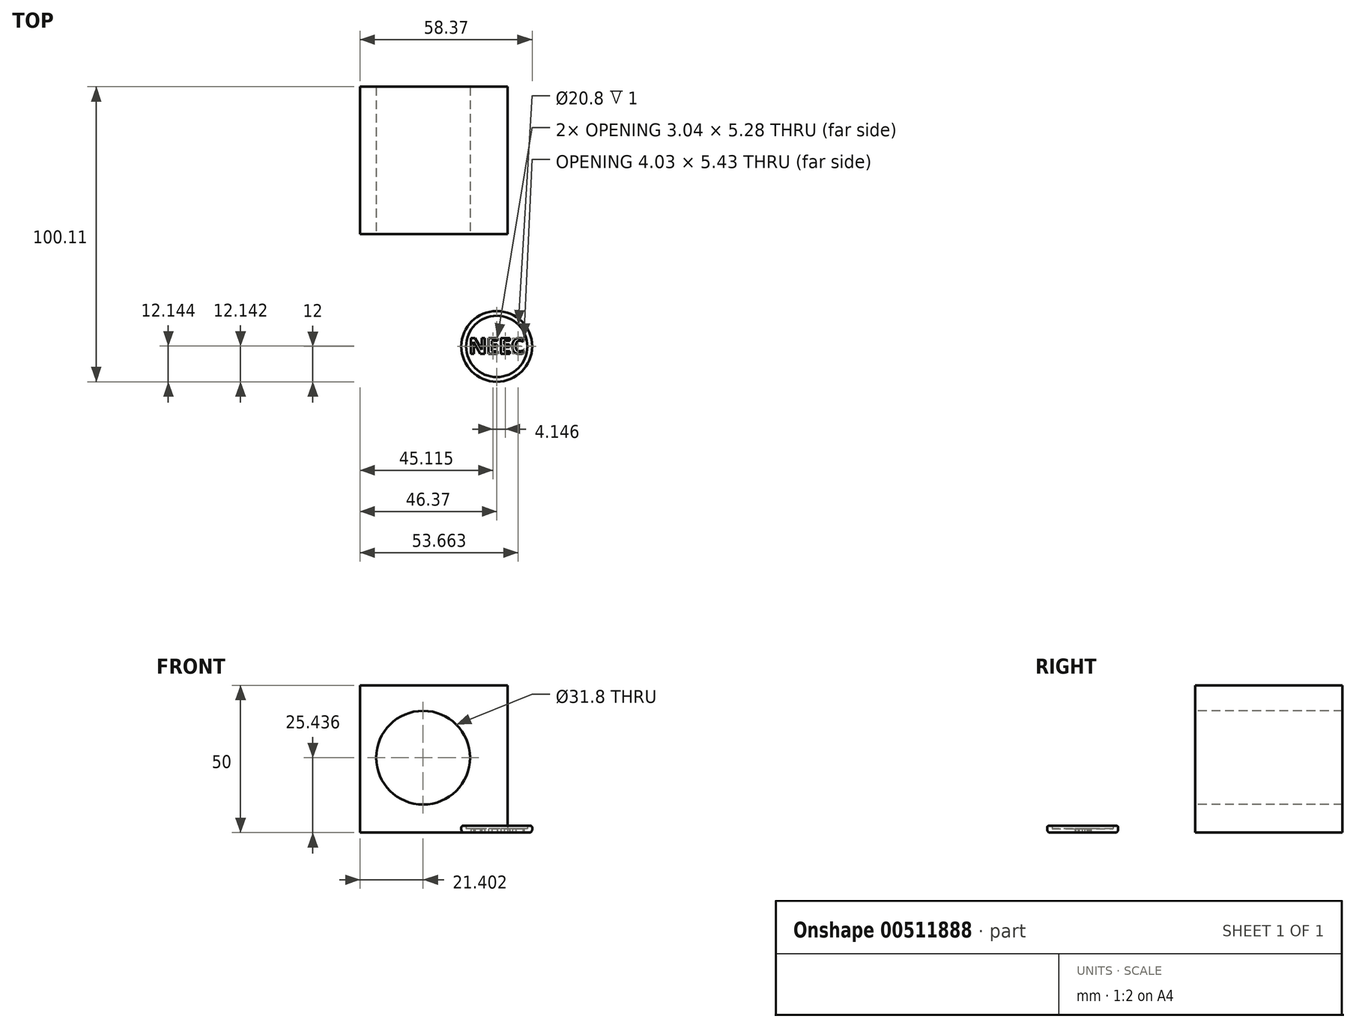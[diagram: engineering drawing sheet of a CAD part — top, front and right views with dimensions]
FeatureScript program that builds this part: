
annotation { "Feature Type Name" : "Feature", "Feature Type Description" : "" }
export const myFeature = defineFeature(function(context is Context, id is Id, definition is map)
    precondition{}
    {
        {
            var Q0;
            Q0=qCreatedBy(makeId("Top.planeOp"),FACE);
            var sketch = newSketch(context, id + "F0", { "sketchPlane" : qUnion([Q0])});
            skCircle(sketch, "E0", {"center": v(0, 0) * mm, "radius": 12 * mm});
            skCircle(sketch, "E1.0", {"center": v(0, 0) * mm, "radius": 10.4 * mm});
            skText(sketch, "E2", { "text": "NEEC", "fontName": "OpenSans-Bold.ttf"});
            const initialGuessF0  = {"E2": [-0.00946, -0.0025, 1, 0, 0.00533]};
            skSetInitialGuess(sketch, initialGuessF0);
            skSolve(sketch);
        }
        {
            var Q0;
            Q0 = qSketchRegion(id + "F0", true);
            extrude(context, id + "F1", {"entities" : qUnion([Q0]), "offsetDistance" : 25 * mm, "depth" : 2.3 * mm});
        }
        {
            var Q0;
            Q0=makeQuery(id+"F0.imprint","IMPRINT",FACE,{"disambiguationData":[TD([[makeQuery(id+"F0.imprint","IMPRINT",EDGE,{"derivedFrom":sQuery(id+"F0.wireOp",EDGE,"E1.0")}),1.0]])]});
            extrude(context, id + "F2", {"entities" : qUnion([Q0]), "operationType" : NewBodyOperationType.ADD, "offsetDistance" : 25 * mm, "depth" : 1.3 * mm});
        }
        {
            var Q0;
            Q0=makeQuery(id+"F1.opExtrude","CAP_EDGE",EDGE,{"disambiguationData":[OSD([sQuery(id+"F0.wireOp",EDGE,"E0")])],"isStart":true});
            fillet(context, id + "F3", {"entities" : qUnion([Q0]), "radius" : 1 * mm, "tangentPropagation" : true, "allowEdgeOverflow" : false});
        }
        {
            var Q0;
            Q0=makeQuery(id+"F1.opExtrude","CAP_EDGE",EDGE,{"disambiguationData":[OSD([sQuery(id+"F0.wireOp",EDGE,"E0")])],"isStart":false});
            fillet(context, id + "F4", {"entities" : qUnion([Q0]), "radius" : 0.5 * mm, "tangentPropagation" : true, "allowEdgeOverflow" : false});
        }
        {
            var Q0;
            Q0=qCreatedBy(makeId("Top.planeOp"),FACE);
            var sketch = newSketch(context, id + "F5", { "sketchPlane" : qUnion([Q0])});
            skLineSegment(sketch, "E3.bottom", {"start": v(-46.37, 88.11) * mm, "end": v(3.63, 88.11) * mm});
            skLineSegment(sketch, "E3.top", {"start": v(-46.37, 38.11) * mm, "end": v(3.63, 38.11) * mm});
            skLineSegment(sketch, "E3.left", {"start": v(-46.37, 88.11) * mm, "end": v(-46.37, 38.11) * mm});
            skLineSegment(sketch, "E3.right", {"start": v(3.63, 88.11) * mm, "end": v(3.63, 38.11) * mm});
            skSolve(sketch);
        }
        {
            var Q0;
            Q0=makeQuery(id+"F5.imprint","IMPRINT",FACE,{"disambiguationData":[TD([[makeQuery(id+"F5.imprint","IMPRINT",EDGE,{"derivedFrom":sQuery(id+"F5.wireOp",EDGE,"E3.bottom")}),-1.0]])]});
            extrude(context, id + "F6", {"entities" : qUnion([Q0]), "depth" : 50 * mm, "offsetDistance" : 25 * mm});
        }
        {
            var Q0;
            Q0=makeQuery(id+"F6.opExtrude","SWEPT_FACE",FACE,{"disambiguationData":[OSD([sQuery(id+"F5.wireOp",EDGE,"E3.top")])]});
            var sketch = newSketch(context, id + "F7", { "sketchPlane" : qUnion([Q0])});
            skCircle(sketch, "E4", {"center": v(-24.97, 25.44) * mm, "radius": 15.9 * mm});
            skSolve(sketch);
        }
        {
            var Q0;
            Q0=makeQuery(id+"F7.imprint","IMPRINT",FACE,{"disambiguationData":[TD([[makeQuery(id+"F7.imprint","IMPRINT",EDGE,{"derivedFrom":sQuery(id+"F7.wireOp",EDGE,"E4")}),1.0]])]});
            extrude(context, id + "F8", {"entities" : qUnion([Q0]), "operationType" : NewBodyOperationType.REMOVE, "oppositeDirection" : true, "depth" : 100 * mm, "offsetDistance" : 25 * mm});
        }
    });
